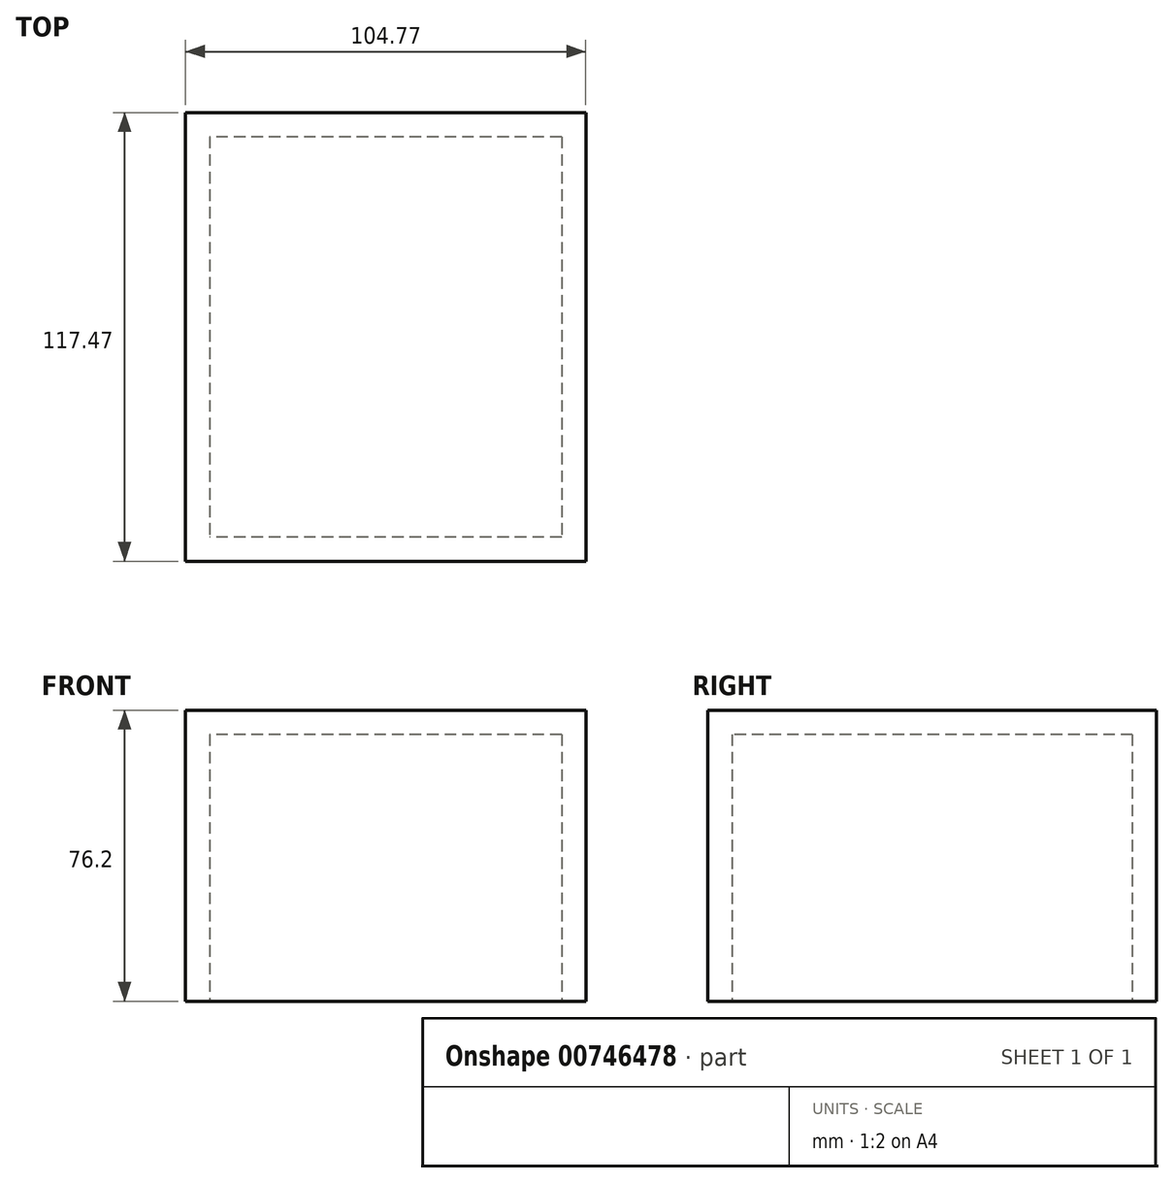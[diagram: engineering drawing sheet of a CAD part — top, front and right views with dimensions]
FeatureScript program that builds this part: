
annotation { "Feature Type Name" : "Feature", "Feature Type Description" : "" }
export const myFeature = defineFeature(function(context is Context, id is Id, definition is map)
    precondition{}
    {
        {
            var Q0;
            Q0=qCreatedBy(makeId("Top.planeOp"),FACE);
            var sketch = newSketch(context, id + "F0", { "sketchPlane" : qUnion([Q0])});
            skLineSegment(sketch, "E0.bottom", {"start": v(0, 0) * mm, "end": v(104.78, 0) * mm});
            skLineSegment(sketch, "E0.top", {"start": v(0, 117.48) * mm, "end": v(104.77, 117.48) * mm});
            skLineSegment(sketch, "E0.left", {"start": v(0, 0) * mm, "end": v(0, 117.48) * mm});
            skLineSegment(sketch, "E0.right", {"start": v(104.78, 0) * mm, "end": v(104.77, 117.47) * mm});
            skLineSegment(sketch, "E1.bottom", {"start": v(98.42, 111.13) * mm, "end": v(6.35, 111.13) * mm});
            skLineSegment(sketch, "E1.top", {"start": v(98.42, 6.35) * mm, "end": v(6.35, 6.35) * mm});
            skLineSegment(sketch, "E1.left", {"start": v(98.42, 111.13) * mm, "end": v(98.42, 6.35) * mm});
            skLineSegment(sketch, "E1.right", {"start": v(6.35, 111.13) * mm, "end": v(6.35, 6.35) * mm});
            skSolve(sketch);
        }
        {
            var Q0;
            Q0=makeQuery(id+"F0.imprint","IMPRINT",FACE,{"disambiguationData":[TD([[makeQuery(id+"F0.imprint","IMPRINT",EDGE,{"derivedFrom":sQuery(id+"F0.wireOp",EDGE,"E0.bottom")}),1.0]])]});
            extrude(context, id + "F1", {"entities" : qUnion([Q0]), "depth" : 69.85 * mm, "offsetDistance" : 25.4 * mm});
        }
        {
            var Q0;
            Q0=makeQuery(id+"F1.opExtrude","CAP_FACE",FACE,{"disambiguationData":[OSD([sQuery(id+"F0.wireOp",EDGE,"E0.bottom"),sQuery(id+"F0.wireOp",EDGE,"E0.top"),sQuery(id+"F0.wireOp",EDGE,"E0.left"),sQuery(id+"F0.wireOp",EDGE,"E0.right"),sQuery(id+"F0.wireOp",EDGE,"E1.bottom"),sQuery(id+"F0.wireOp",EDGE,"E1.top"),sQuery(id+"F0.wireOp",EDGE,"E1.left"),sQuery(id+"F0.wireOp",EDGE,"E1.right")])],"isStart":false});
            var sketch = newSketch(context, id + "F2", { "sketchPlane" : qUnion([Q0])});
            skLineSegment(sketch, "E2.bottom", {"start": v(0, 117.48) * mm, "end": v(104.78, 117.48) * mm});
            skLineSegment(sketch, "E2.top", {"start": v(0, 0) * mm, "end": v(104.78, 0) * mm});
            skLineSegment(sketch, "E2.left", {"start": v(0, 117.48) * mm, "end": v(0, 0) * mm});
            skLineSegment(sketch, "E2.right", {"start": v(104.78, 117.48) * mm, "end": v(104.78, 0) * mm});
            skSolve(sketch);
        }
        {
            var Q0;
            Q0=makeQuery(id+"F2.imprint","IMPRINT",FACE,{"disambiguationData":[TD([[makeQuery(id+"F2.imprint","IMPRINT",EDGE,{"derivedFrom":makeQuery(id+"F1.opExtrude","CAP_EDGE",EDGE,{"disambiguationData":[OSD([sQuery(id+"F0.wireOp",EDGE,"E1.bottom")])],"isStart":false})}),1.0]])]});
            var Q1;
            Q1=makeQuery(id+"F2.imprint","IMPRINT",FACE,{"disambiguationData":[TD([[makeQuery(id+"F2.imprint","IMPRINT",EDGE,{"derivedFrom":sQuery(id+"F2.wireOp",EDGE,"E2.bottom")}),-1.0]])]});
            extrude(context, id + "F3", {"entities" : qUnion([Q0, Q1]), "operationType" : NewBodyOperationType.ADD, "depth" : 6.35 * mm, "offsetDistance" : 25.4 * mm});
        }
    });
